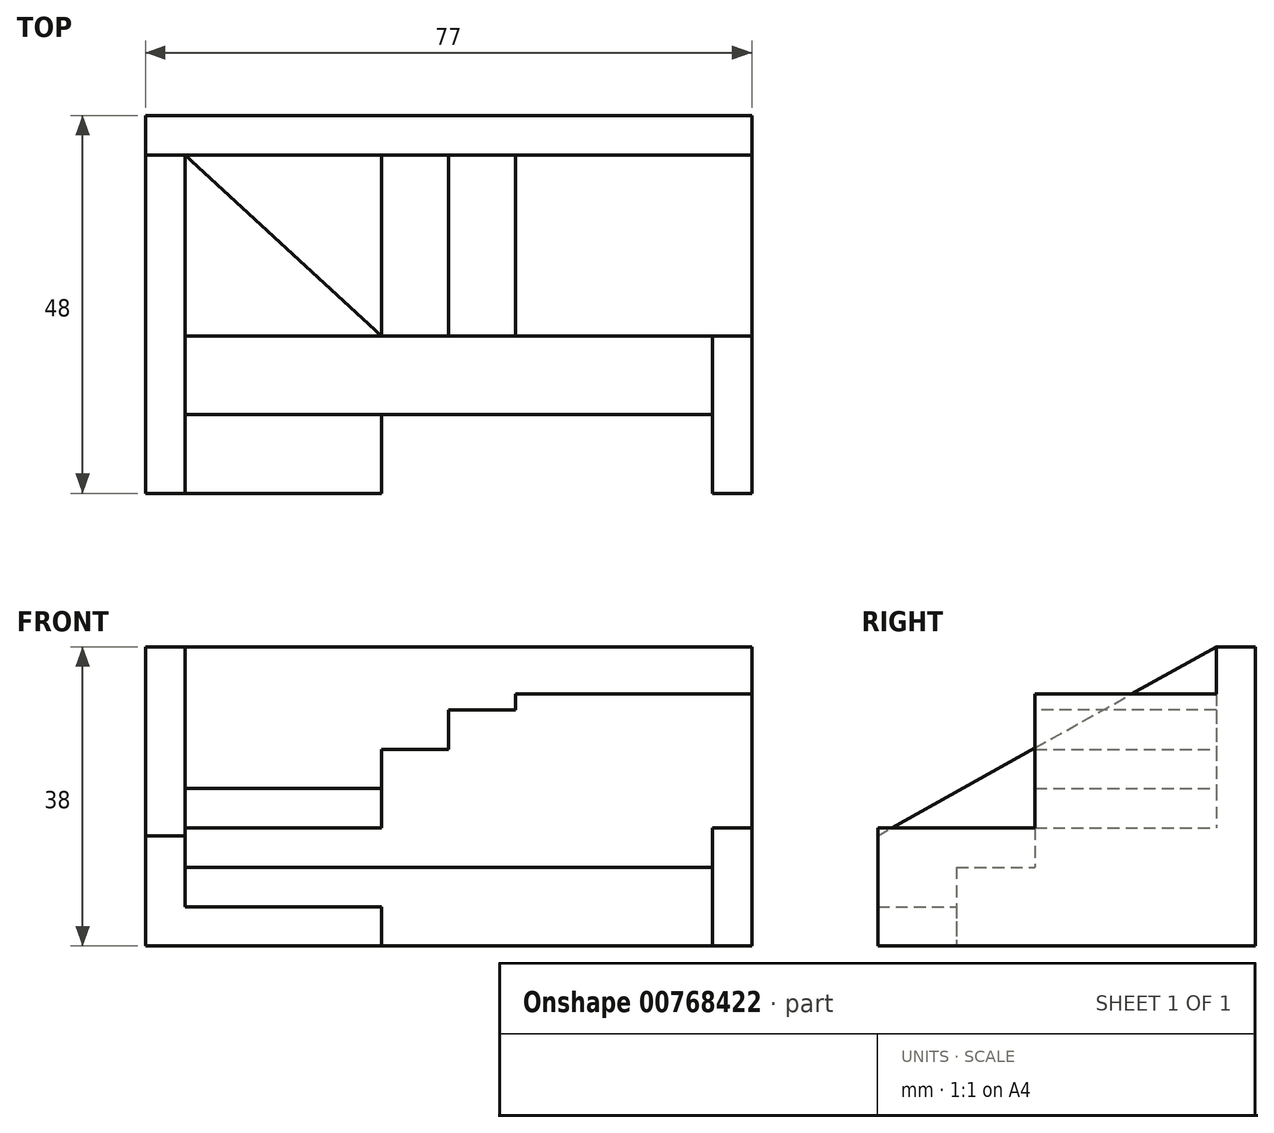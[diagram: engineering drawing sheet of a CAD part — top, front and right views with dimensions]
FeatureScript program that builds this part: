
annotation { "Feature Type Name" : "Feature", "Feature Type Description" : "" }
export const myFeature = defineFeature(function(context is Context, id is Id, definition is map)
    precondition{}
    {
        {
            var Q0;
            Q0=qCreatedBy(makeId("Top.planeOp"),FACE);
            var sketch = newSketch(context, id + "F0", { "sketchPlane" : qUnion([Q0])});
            skLineSegment(sketch, "E0.bottom", {"start": v(38.5, 24) * mm, "end": v(-38.5, 24) * mm});
            skLineSegment(sketch, "E0.top", {"start": v(38.5, -24) * mm, "end": v(33.5, -24) * mm});
            skLineSegment(sketch, "E0.left", {"start": v(38.5, 24) * mm, "end": v(38.5, -24) * mm});
            skLineSegment(sketch, "E0.right", {"start": v(-38.5, 24) * mm, "end": v(-38.5, -24) * mm});
            skPoint(sketch, "E0.middle", {"position": v(0, 0) * mm});
            skLineSegment(sketch, "E1", {"start": v(-38.5, 19) * mm, "end": v(38.5, 19) * mm});
            skLineSegment(sketch, "E2", {"start": v(0, 19) * mm, "end": v(0, -4) * mm});
            skLineSegment(sketch, "E3", {"start": v(-33.5, -4) * mm, "end": v(38.5, -4) * mm});
            skPoint(sketch, "E4.end.orphan", {"position": v(0, -4) * mm});
            skLineSegment(sketch, "E5", {"start": v(-33.5, -24) * mm, "end": v(-33.5, 19) * mm});
            skPoint(sketch, "E6.orphan", {"position": v(-38.5, -4) * mm});
            skLineSegment(sketch, "E7", {"start": v(-8.5, -24) * mm, "end": v(-8.5, -14) * mm});
            skLineSegment(sketch, "E8", {"start": v(-8.5, -4) * mm, "end": v(-8.5, 19) * mm});
            skLineSegment(sketch, "E9", {"start": v(8.5, -4) * mm, "end": v(8.5, 19) * mm});
            skLineSegment(sketch, "E10", {"start": v(33.5, 24) * mm, "end": v(33.5, -24) * mm});
            skLineSegment(sketch, "E11.trimOffspring", {"start": v(-8.5, -24) * mm, "end": v(-38.5, -24) * mm});
            skLineSegment(sketch, "E12.trimOffspring", {"start": v(-8.5, -14) * mm, "end": v(-33.5, -14) * mm});
            skPoint(sketch, "E13.orphan", {"position": v(0, 24) * mm});
            skPoint(sketch, "E14.start.orphan", {"position": v(38.5, -14) * mm});
            skLineSegment(sketch, "E15", {"start": v(-33.5, -14) * mm, "end": v(33.5, -14) * mm});
            skLineSegment(sketch, "E16", {"start": v(-8.5, -4) * mm, "end": v(-33.5, 19) * mm});
            skSolve(sketch);
        }
        {
            var Q0;
            {var subQ3=sQuery(id+"F0.wireOp",EDGE,"E11.trimOffspring");var subQ5=sQuery(id+"F0.wireOp",EDGE,"E0.right");var subQ6=makeQuery(id+"F0.imprint","INTERSECT",VERTEX,{"derivedFrom":[subQ5,subQ3]});Q0=makeQuery(id+"F0.imprint","IMPRINT",FACE,{"disambiguationData":[TD([[makeQuery(id+"F0.imprint","IMPRINT",EDGE,{"disambiguationData":[TD([[subQ6,1.0]])],"derivedFrom":subQ5}),1.0]])]});}
            extrude(context, id + "F1", {"entities" : qUnion([Q0]), "depth" : 38 * mm, "offsetDistance" : 25 * mm});
        }
        {
            var Q0;
            Q0=makeQuery(id+"F1.opExtrude","SWEPT_FACE",FACE,{"disambiguationData":[OSD([sQuery(id+"F0.wireOp",EDGE,"E5")])]});
            var sketch = newSketch(context, id + "F2", { "sketchPlane" : qUnion([Q0])});
            skLineSegment(sketch, "E17", {"start": v(-24, 14) * mm, "end": v(19, 38) * mm});
            skSolve(sketch);
        }
        {
            var Q0;
            {var subQ0=sQuery(id+"F2.wireOp",EDGE,"E17");Q0=makeQuery(id+"F2.imprint","IMPRINT",FACE,{"disambiguationData":[TD([[makeQuery(id+"F2.imprint","IMPRINT",EDGE,{"derivedFrom":subQ0}),1.0]])]});}
            extrude(context, id + "F3", {"entities" : qUnion([Q0]), "operationType" : NewBodyOperationType.REMOVE, "oppositeDirection" : true, "depth" : 25 * mm, "offsetDistance" : 25 * mm});
        }
        {
            var Q0;
            Q0 = qSketchRegion(id + "F2", true);
            var Q1;
            {var subQ3=sQuery(id+"F0.wireOp",EDGE,"E0.right");var subQ5=sQuery(id+"F0.wireOp",EDGE,"E0.bottom");var subQ6=makeQuery(id+"F0.imprint","INTERSECT",VERTEX,{"derivedFrom":[subQ5,subQ3]});Q1=makeQuery(id+"F0.imprint","IMPRINT",FACE,{"disambiguationData":[TD([[makeQuery(id+"F0.imprint","IMPRINT",EDGE,{"disambiguationData":[TD([[subQ6,1.0]])],"derivedFrom":subQ5}),1.0]])]});}
            extrude(context, id + "F4", {"entities" : qUnion([Q0, Q1]), "operationType" : NewBodyOperationType.ADD, "depth" : 38 * mm, "offsetDistance" : 25 * mm});
        }
        {
            var Q0;
            {var subQ5=sQuery(id+"F0.wireOp",EDGE,"E7");Q0=makeQuery(id+"F0.imprint","IMPRINT",FACE,{"disambiguationData":[TD([[makeQuery(id+"F0.imprint","IMPRINT",EDGE,{"derivedFrom":subQ5}),1.0]])]});}
            extrude(context, id + "F5", {"entities" : qUnion([Q0]), "operationType" : NewBodyOperationType.ADD, "depth" : 5 * mm, "offsetDistance" : 25 * mm});
        }
        {
            var Q0;
            {var subQ0=sQuery(id+"F0.wireOp",EDGE,"E3");var subQ4=makeQuery(id+"F0.imprint","INTERSECT",VERTEX,{"derivedFrom":[sQuery(id+"F0.wireOp",EDGE,"E2"),subQ0]});Q0=makeQuery(id+"F0.imprint","IMPRINT",FACE,{"disambiguationData":[TD([[makeQuery(id+"F0.imprint","IMPRINT",EDGE,{"disambiguationData":[TD([[subQ4,-1.0]])],"derivedFrom":subQ0}),-1.0]])]});}
            extrude(context, id + "F6", {"entities" : qUnion([Q0]), "operationType" : NewBodyOperationType.ADD, "depth" : 10 * mm, "offsetDistance" : 25 * mm});
        }
        {
            var Q0;
            {var subQ6=sQuery(id+"F0.wireOp",EDGE,"E0.top");Q0=makeQuery(id+"F0.imprint","IMPRINT",FACE,{"disambiguationData":[TD([[makeQuery(id+"F0.imprint","IMPRINT",EDGE,{"derivedFrom":subQ6}),-1.0]])]});}
            extrude(context, id + "F7", {"entities" : qUnion([Q0]), "operationType" : NewBodyOperationType.ADD, "depth" : 15 * mm, "offsetDistance" : 25 * mm});
        }
        {
            var Q0;
            {var subQ0=sQuery(id+"F0.wireOp",EDGE,"E0.left");var subQ1=sQuery(id+"F0.wireOp",EDGE,"E0.bottom");var subQ2=makeQuery(id+"F0.imprint","INTERSECT",VERTEX,{"derivedFrom":[subQ1,subQ0]});Q0=makeQuery(id+"F0.imprint","IMPRINT",FACE,{"disambiguationData":[TD([[makeQuery(id+"F0.imprint","IMPRINT",EDGE,{"disambiguationData":[TD([[subQ2,-1.0]])],"derivedFrom":subQ1}),1.0]])]});}
            extrude(context, id + "F8", {"entities" : qUnion([Q0]), "operationType" : NewBodyOperationType.ADD, "depth" : 38 * mm, "offsetDistance" : 25 * mm});
        }
        {
            var Q0;
            {var subQ0=sQuery(id+"F0.wireOp",EDGE,"E1");var subQ1=sQuery(id+"F0.wireOp",EDGE,"E0.left");var subQ2=makeQuery(id+"F0.imprint","INTERSECT",VERTEX,{"derivedFrom":[subQ1,subQ0]});Q0=makeQuery(id+"F0.imprint","IMPRINT",FACE,{"disambiguationData":[TD([[makeQuery(id+"F0.imprint","IMPRINT",EDGE,{"disambiguationData":[TD([[subQ2,-1.0]])],"derivedFrom":subQ1}),-1.0]])]});}
            extrude(context, id + "F9", {"entities" : qUnion([Q0]), "operationType" : NewBodyOperationType.ADD, "depth" : 32 * mm, "offsetDistance" : 25 * mm});
        }
        {
            var Q0;
            Q0=sQuery(id+"F0.wireOp",EDGE,"E0.bottom");
            extrude(context, id + "F10", {"bodyType" : ToolBodyType.SURFACE, "surfaceEntities" : qUnion([Q0]), "depth" : 25 * mm, "offsetDistance" : 25 * mm});
        }
        {
            var Q0;
            {var subQ3=sQuery(id+"F0.wireOp",EDGE,"E16");Q0=makeQuery(id+"F0.imprint","IMPRINT",FACE,{"disambiguationData":[TD([[makeQuery(id+"F0.imprint","IMPRINT",EDGE,{"derivedFrom":subQ3}),1.0]])]});}
            extrude(context, id + "F11", {"entities" : qUnion([Q0]), "operationType" : NewBodyOperationType.ADD, "depth" : 15 * mm, "offsetDistance" : 25 * mm});
        }
        {
            var Q0;
            {var subQ2=sQuery(id+"F0.wireOp",EDGE,"E8");Q0=makeQuery(id+"F0.imprint","IMPRINT",FACE,{"disambiguationData":[TD([[makeQuery(id+"F0.imprint","IMPRINT",EDGE,{"derivedFrom":subQ2}),1.0]])]});}
            extrude(context, id + "F12", {"entities" : qUnion([Q0]), "operationType" : NewBodyOperationType.ADD, "depth" : 20 * mm, "offsetDistance" : 25 * mm});
        }
        {
            var Q0;
            {var subQ0=sQuery(id+"F0.wireOp",EDGE,"E2");Q0=makeQuery(id+"F0.imprint","IMPRINT",FACE,{"disambiguationData":[TD([[makeQuery(id+"F0.imprint","IMPRINT",EDGE,{"derivedFrom":subQ0}),-1.0]])]});}
            extrude(context, id + "F13", {"entities" : qUnion([Q0]), "operationType" : NewBodyOperationType.ADD, "depth" : 25 * mm, "offsetDistance" : 25 * mm});
        }
        {
            var Q0;
            {var subQ0=sQuery(id+"F0.wireOp",EDGE,"E2");Q0=makeQuery(id+"F0.imprint","IMPRINT",FACE,{"disambiguationData":[TD([[makeQuery(id+"F0.imprint","IMPRINT",EDGE,{"derivedFrom":subQ0}),1.0]])]});}
            extrude(context, id + "F14", {"entities" : qUnion([Q0]), "operationType" : NewBodyOperationType.ADD, "depth" : 30 * mm, "offsetDistance" : 25 * mm});
        }
        {
            var Q0;
            {var subQ0=sQuery(id+"F0.wireOp",EDGE,"E9");Q0=makeQuery(id+"F0.imprint","IMPRINT",FACE,{"disambiguationData":[TD([[makeQuery(id+"F0.imprint","IMPRINT",EDGE,{"derivedFrom":subQ0}),-1.0]])]});}
            extrude(context, id + "F15", {"entities" : qUnion([Q0]), "operationType" : NewBodyOperationType.ADD, "depth" : 32 * mm, "offsetDistance" : 25 * mm});
        }
    });
